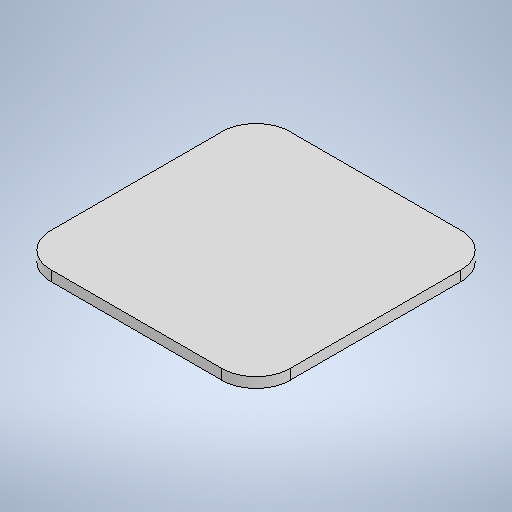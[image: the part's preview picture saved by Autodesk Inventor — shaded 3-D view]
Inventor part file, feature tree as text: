
AUTODESK INVENTOR PART (.ipt)
format: ipt  version: 2025 (Build 290162010, 162A)  size: 250,880 bytes
history: native  units: mm
features: other x2, sheet_metal_op x1, chamfer x1, sketch x1
ambient origin geometry x8: Origin, YZ Plane, XZ Plane, XY Plane, X Axis, Y Axis, Z Axis, Center Point
bodies: Solid1 (feature_tree)
feature tree (5):
  sheet_metal_op  "Face1"
  chamfer  "Corner Round1"
  sketch  "Sketch1"  dims[d0=140.0mm d1=140.0mm d2=6.0mm d22=20.0mm]
  other  "Plate1"
  other  "Definition1"
